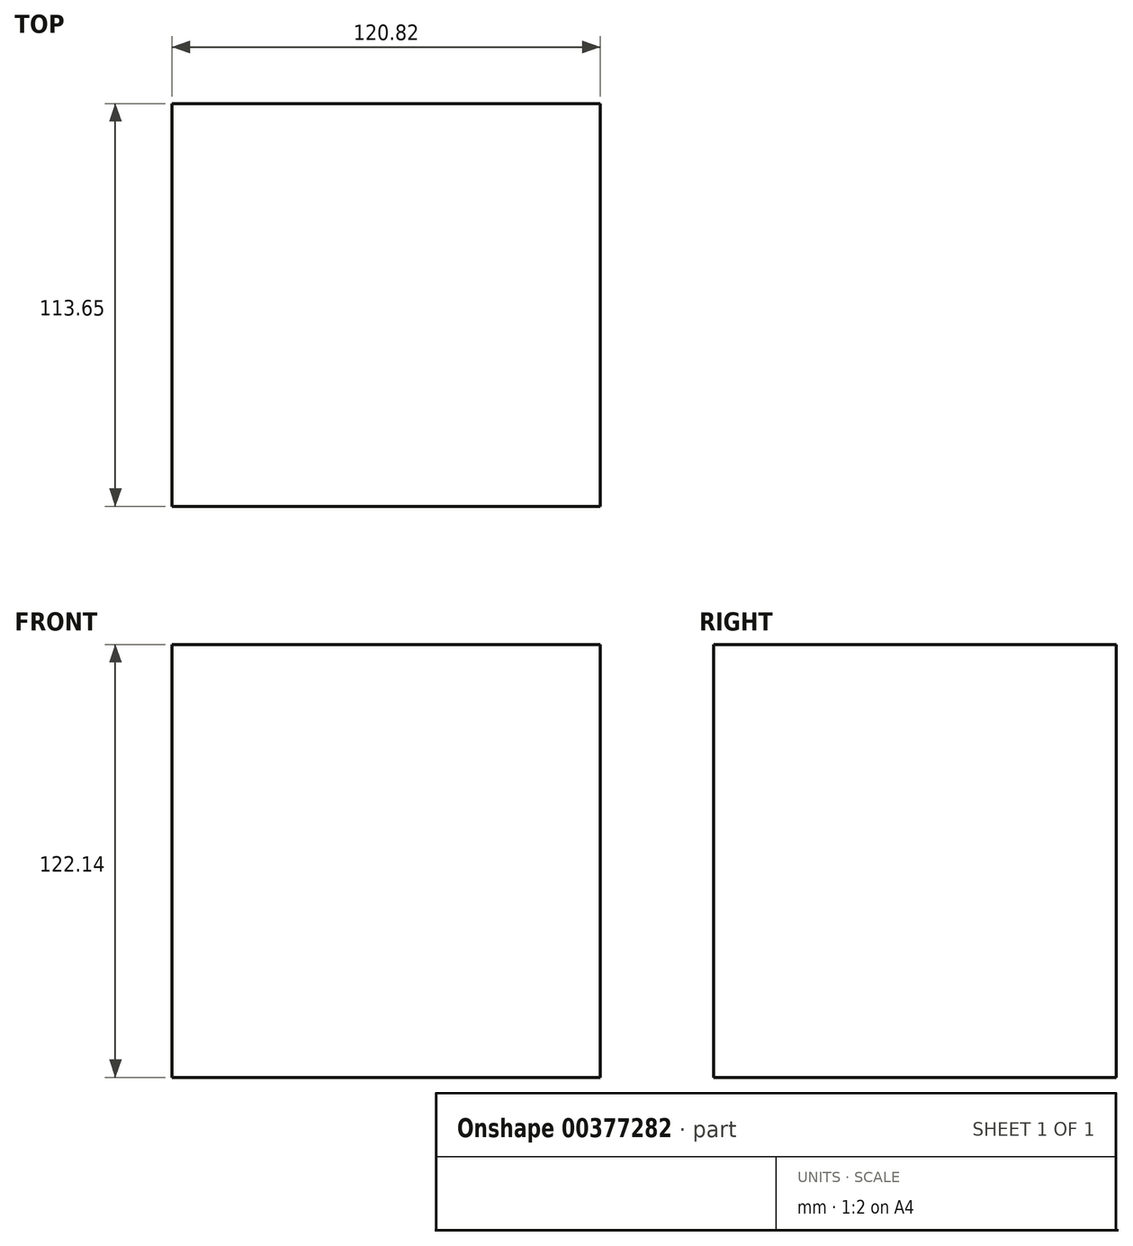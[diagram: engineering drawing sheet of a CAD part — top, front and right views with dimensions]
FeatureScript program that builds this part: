
annotation { "Feature Type Name" : "Feature", "Feature Type Description" : "" }
export const myFeature = defineFeature(function(context is Context, id is Id, definition is map)
    precondition{}
    {
        {
            var Q0;
            Q0=qCreatedBy(makeId("Front.planeOp"),FACE);
            var sketch = newSketch(context, id + "F0", { "sketchPlane" : qUnion([Q0])});
            skLineSegment(sketch, "E0.bottom", {"start": v(50.06, -33.97) * mm, "end": v(-70.76, -33.97) * mm});
            skLineSegment(sketch, "E0.top", {"start": v(50.06, 88.17) * mm, "end": v(-70.76, 88.17) * mm});
            skLineSegment(sketch, "E0.left", {"start": v(50.06, -33.97) * mm, "end": v(50.06, 88.17) * mm});
            skLineSegment(sketch, "E0.right", {"start": v(-70.76, -33.97) * mm, "end": v(-70.76, 88.17) * mm});
            skSolve(sketch);
        }
        {
            var Q0;
            Q0 = qSketchRegion(id + "F0", true);
            extrude(context, id + "F1", {"entities" : qUnion([Q0]), "depth" : 113.65 * mm});
        }
    });
